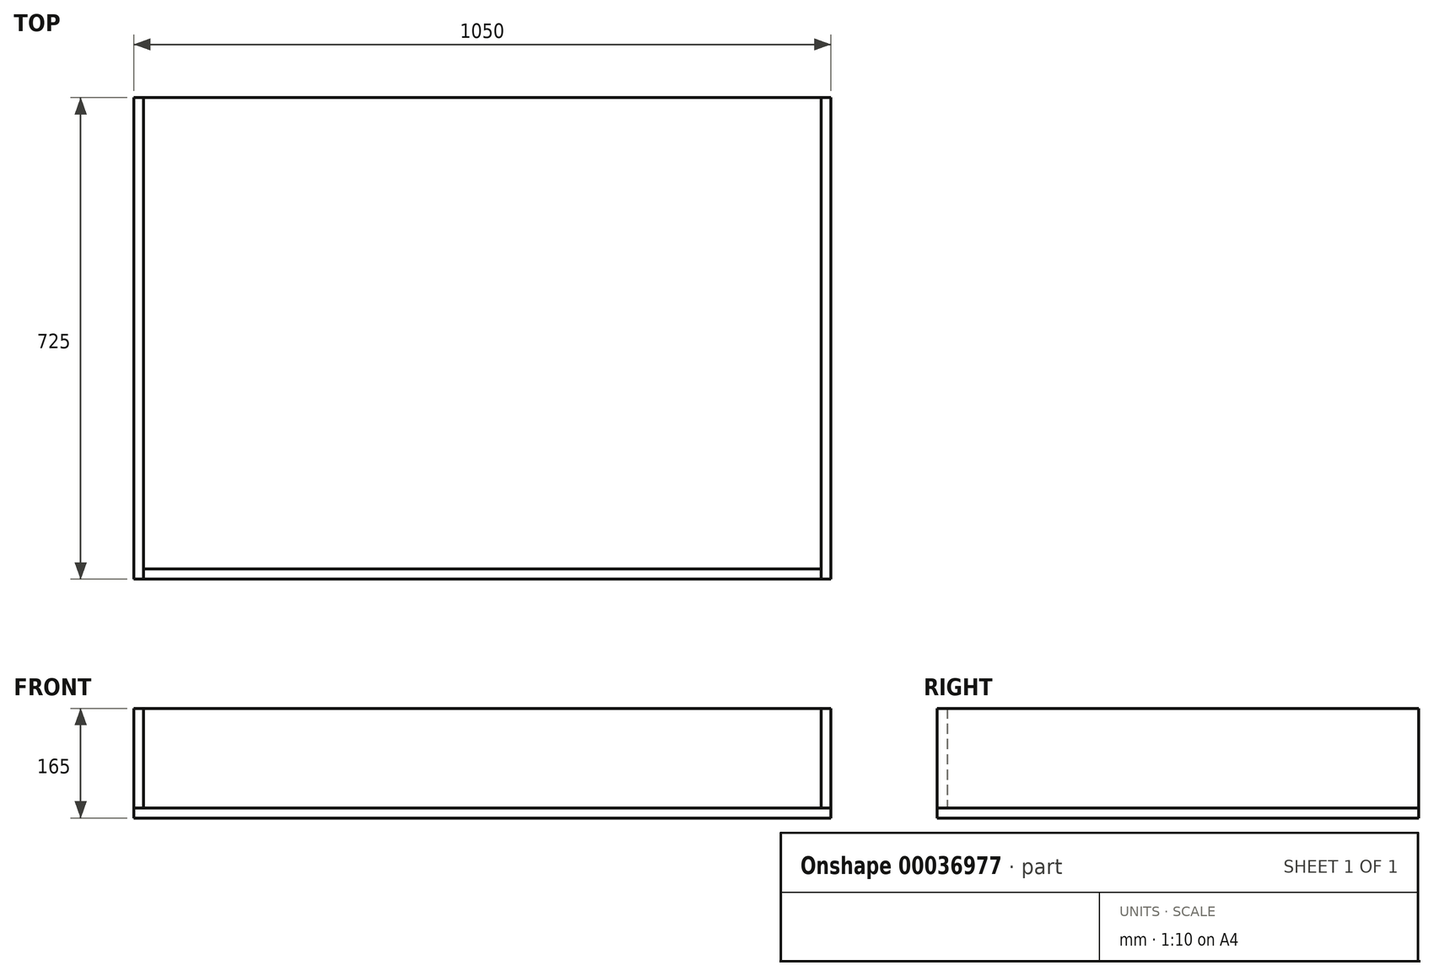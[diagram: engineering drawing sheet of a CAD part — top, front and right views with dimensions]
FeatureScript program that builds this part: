
annotation { "Feature Type Name" : "Feature", "Feature Type Description" : "" }
export const myFeature = defineFeature(function(context is Context, id is Id, definition is map)
    precondition{}
    {
        {
            var Q0;
            Q0=qCreatedBy(makeId("Top.planeOp"),FACE);
            var sketch = newSketch(context, id + "F0", { "sketchPlane" : qUnion([Q0])});
            skLineSegment(sketch, "E0.rect.bottom", {"start": v(525, -362.5) * mm, "end": v(-525, -362.5) * mm});
            skLineSegment(sketch, "E0.rect.top", {"start": v(525, 362.5) * mm, "end": v(-525, 362.5) * mm});
            skLineSegment(sketch, "E0.rect.left", {"start": v(525, -362.5) * mm, "end": v(525, 362.5) * mm});
            skLineSegment(sketch, "E0.rect.right", {"start": v(-525, -362.5) * mm, "end": v(-525, 362.5) * mm});
            skPoint(sketch, "E0.rect.middle", {"position": v(0, 0) * mm});
            skLineSegment(sketch, "E1.0", {"start": v(-510, -362.5) * mm, "end": v(-510, 362.5) * mm});
            skLineSegment(sketch, "E2.0", {"start": v(525, -347.5) * mm, "end": v(-525, -347.5) * mm});
            skLineSegment(sketch, "E3.0", {"start": v(540, -719.64) * mm, "end": v(540, -707.16) * mm});
            skLineSegment(sketch, "E4.0", {"start": v(540, -645.7) * mm, "end": v(540, -494.87) * mm});
            skLineSegment(sketch, "E5.0", {"start": v(510, -362.5) * mm, "end": v(510, 362.5) * mm});
            skSolve(sketch);
        }
        {
            var Q0;
            {var subQ3=sQuery(id+"F0.wireOp",EDGE,"E0.rect.right");var subQ5=sQuery(id+"F0.wireOp",EDGE,"E0.rect.top");var subQ7=makeQuery(id+"F0.imprint","INTERSECT",VERTEX,{"derivedFrom":[subQ5,subQ3]});Q0=makeQuery(id+"F0.imprint","IMPRINT",FACE,{"disambiguationData":[TD([[makeQuery(id+"F0.imprint","IMPRINT",EDGE,{"disambiguationData":[TD([[subQ7,1.0]])],"derivedFrom":subQ5}),1.0]])]});}
            var Q1;
            {var subQ3=sQuery(id+"F0.wireOp",EDGE,"E0.rect.right");var subQ5=sQuery(id+"F0.wireOp",EDGE,"E0.rect.bottom");var subQ7=makeQuery(id+"F0.imprint","INTERSECT",VERTEX,{"derivedFrom":[subQ5,subQ3]});Q1=makeQuery(id+"F0.imprint","IMPRINT",FACE,{"disambiguationData":[TD([[makeQuery(id+"F0.imprint","IMPRINT",EDGE,{"disambiguationData":[TD([[subQ7,1.0]])],"derivedFrom":subQ5}),-1.0]])]});}
            extrude(context, id + "F3", {"entities" : qUnion([Q0, Q1]), "depth" : 150 * mm});
        }
        {
            var Q0;
            {var subQ3=sQuery(id+"F0.wireOp",EDGE,"E0.rect.bottom");var subQ5=sQuery(id+"F0.wireOp",EDGE,"E1.0");var subQ7=makeQuery(id+"F0.imprint","INTERSECT",VERTEX,{"derivedFrom":[subQ3,subQ5]});Q0=makeQuery(id+"F0.imprint","IMPRINT",FACE,{"disambiguationData":[TD([[makeQuery(id+"F0.imprint","IMPRINT",EDGE,{"disambiguationData":[TD([[subQ7,1.0]])],"derivedFrom":subQ3}),-1.0]])]});}
            extrude(context, id + "F1", {"entities" : qUnion([Q0]), "depth" : 150 * mm});
        }
        {
            var Q0;
            {var subQ3=sQuery(id+"F0.wireOp",EDGE,"E0.rect.top");var subQ5=sQuery(id+"F0.wireOp",EDGE,"E0.rect.left");var subQ7=makeQuery(id+"F0.imprint","INTERSECT",VERTEX,{"derivedFrom":[subQ3,subQ5]});Q0=makeQuery(id+"F0.imprint","IMPRINT",FACE,{"disambiguationData":[TD([[makeQuery(id+"F0.imprint","IMPRINT",EDGE,{"disambiguationData":[TD([[subQ7,-1.0]])],"derivedFrom":subQ3}),1.0]])]});}
            var Q1;
            {var subQ3=sQuery(id+"F0.wireOp",EDGE,"E0.rect.bottom");var subQ5=sQuery(id+"F0.wireOp",EDGE,"E0.rect.left");var subQ7=makeQuery(id+"F0.imprint","INTERSECT",VERTEX,{"derivedFrom":[subQ3,subQ5]});Q1=makeQuery(id+"F0.imprint","IMPRINT",FACE,{"disambiguationData":[TD([[makeQuery(id+"F0.imprint","IMPRINT",EDGE,{"disambiguationData":[TD([[subQ7,-1.0]])],"derivedFrom":subQ3}),-1.0]])]});}
            extrude(context, id + "F2", {"entities" : qUnion([Q0, Q1]), "depth" : 150 * mm});
        }
        {
            var Q0;
            {var subQ3=sQuery(id+"F0.wireOp",EDGE,"E0.rect.top");var subQ5=sQuery(id+"F0.wireOp",EDGE,"E1.0");var subQ7=makeQuery(id+"F0.imprint","INTERSECT",VERTEX,{"derivedFrom":[subQ3,subQ5]});Q0=makeQuery(id+"F0.imprint","IMPRINT",FACE,{"disambiguationData":[TD([[makeQuery(id+"F0.imprint","IMPRINT",EDGE,{"disambiguationData":[TD([[subQ7,1.0]])],"derivedFrom":subQ3}),1.0]])]});}
            var Q1;
            {var subQ3=sQuery(id+"F0.wireOp",EDGE,"E0.rect.right");var subQ5=sQuery(id+"F0.wireOp",EDGE,"E0.rect.top");var subQ7=makeQuery(id+"F0.imprint","INTERSECT",VERTEX,{"derivedFrom":[subQ5,subQ3]});Q1=makeQuery(id+"F0.imprint","IMPRINT",FACE,{"disambiguationData":[TD([[makeQuery(id+"F0.imprint","IMPRINT",EDGE,{"disambiguationData":[TD([[subQ7,1.0]])],"derivedFrom":subQ5}),1.0]])]});}
            var Q2;
            {var subQ3=sQuery(id+"F0.wireOp",EDGE,"E0.rect.bottom");var subQ5=sQuery(id+"F0.wireOp",EDGE,"E1.0");var subQ7=makeQuery(id+"F0.imprint","INTERSECT",VERTEX,{"derivedFrom":[subQ3,subQ5]});Q2=makeQuery(id+"F0.imprint","IMPRINT",FACE,{"disambiguationData":[TD([[makeQuery(id+"F0.imprint","IMPRINT",EDGE,{"disambiguationData":[TD([[subQ7,1.0]])],"derivedFrom":subQ3}),-1.0]])]});}
            var Q3;
            {var subQ3=sQuery(id+"F0.wireOp",EDGE,"E0.rect.right");var subQ5=sQuery(id+"F0.wireOp",EDGE,"E0.rect.bottom");var subQ7=makeQuery(id+"F0.imprint","INTERSECT",VERTEX,{"derivedFrom":[subQ5,subQ3]});Q3=makeQuery(id+"F0.imprint","IMPRINT",FACE,{"disambiguationData":[TD([[makeQuery(id+"F0.imprint","IMPRINT",EDGE,{"disambiguationData":[TD([[subQ7,1.0]])],"derivedFrom":subQ5}),-1.0]])]});}
            var Q4;
            {var subQ3=sQuery(id+"F0.wireOp",EDGE,"E0.rect.bottom");var subQ5=sQuery(id+"F0.wireOp",EDGE,"E1.0");var subQ7=makeQuery(id+"F0.imprint","INTERSECT",VERTEX,{"derivedFrom":[subQ3,subQ5]});Q4=makeQuery(id+"F0.imprint","IMPRINT",FACE,{"disambiguationData":[TD([[makeQuery(id+"F0.imprint","IMPRINT",EDGE,{"disambiguationData":[TD([[subQ7,1.0]])],"derivedFrom":subQ3}),-1.0]])]});}
            var Q5;
            {var subQ3=sQuery(id+"F0.wireOp",EDGE,"E0.rect.top");var subQ5=sQuery(id+"F0.wireOp",EDGE,"E0.rect.left");var subQ7=makeQuery(id+"F0.imprint","INTERSECT",VERTEX,{"derivedFrom":[subQ3,subQ5]});Q5=makeQuery(id+"F0.imprint","IMPRINT",FACE,{"disambiguationData":[TD([[makeQuery(id+"F0.imprint","IMPRINT",EDGE,{"disambiguationData":[TD([[subQ7,-1.0]])],"derivedFrom":subQ3}),1.0]])]});}
            var Q6;
            {var subQ3=sQuery(id+"F0.wireOp",EDGE,"E0.rect.bottom");var subQ5=sQuery(id+"F0.wireOp",EDGE,"E0.rect.left");var subQ7=makeQuery(id+"F0.imprint","INTERSECT",VERTEX,{"derivedFrom":[subQ3,subQ5]});Q6=makeQuery(id+"F0.imprint","IMPRINT",FACE,{"disambiguationData":[TD([[makeQuery(id+"F0.imprint","IMPRINT",EDGE,{"disambiguationData":[TD([[subQ7,-1.0]])],"derivedFrom":subQ3}),-1.0]])]});}
            extrude(context, id + "F4", {"entities" : qUnion([Q0, Q1, Q2, Q3, Q4, Q5, Q6]), "oppositeDirection" : true, "depth" : 15 * mm});
        }
    });
